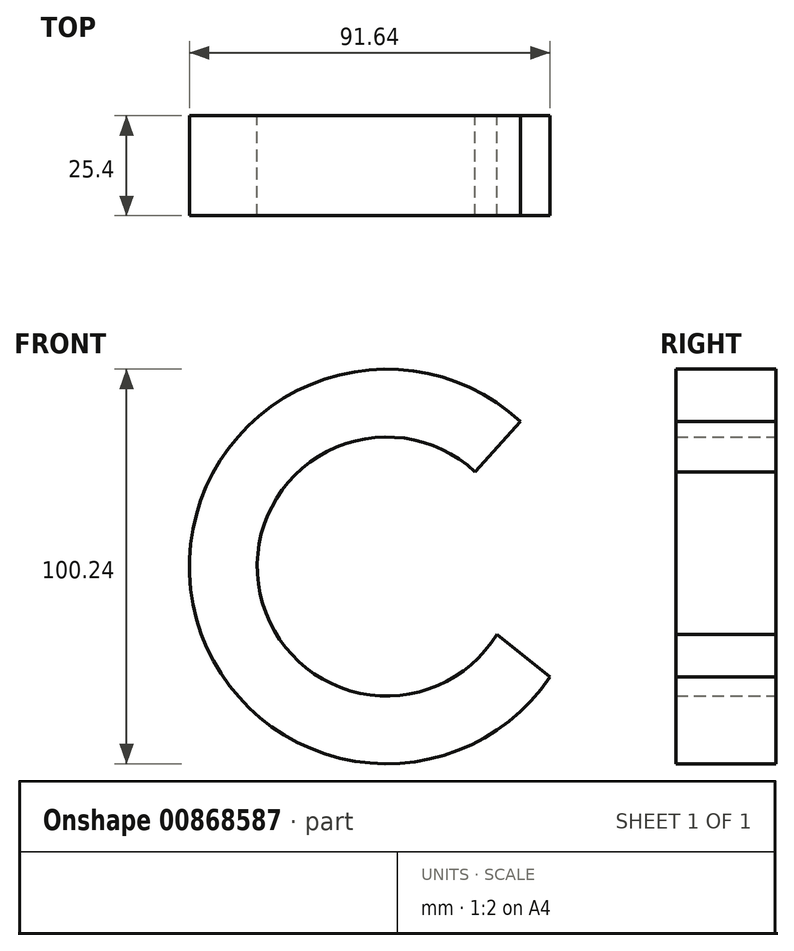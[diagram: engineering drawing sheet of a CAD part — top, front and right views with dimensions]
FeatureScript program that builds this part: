
annotation { "Feature Type Name" : "Feature", "Feature Type Description" : "" }
export const myFeature = defineFeature(function(context is Context, id is Id, definition is map)
    precondition{}
    {
        {
            var Q0;
            Q0=qCreatedBy(makeId("Front.planeOp"),FACE);
            var sketch = newSketch(context, id + "F0", { "sketchPlane" : qUnion([Q0])});
            skArc(sketch, "E0", {"start": v(33.94, 36.89) * mm, "mid": v(-49.78, -5.81) * mm, "end": v(41.52, -28.08) * mm});
            skArc(sketch, "E1", {"start": v(22.45, 24.04) * mm, "mid": v(-32.6, -4.42) * mm, "end": v(28.04, -17.2) * mm});
            skLineSegment(sketch, "E2", {"start": v(22.45, 24.04) * mm, "end": v(33.94, 36.89) * mm});
            skLineSegment(sketch, "E3", {"start": v(28.04, -17.2) * mm, "end": v(41.52, -28.08) * mm});
            skSolve(sketch);
        }
        {
            var Q0;
            Q0 = qSketchRegion(id + "F0", true);
            extrude(context, id + "F1", {"entities" : qUnion([Q0]), "depth" : 25.4 * mm, "offsetDistance" : 25.4 * mm});
        }
    });
